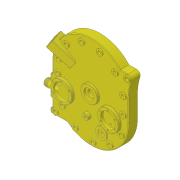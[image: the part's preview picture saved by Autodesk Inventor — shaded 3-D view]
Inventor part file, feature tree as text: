
AUTODESK INVENTOR PART (.ipt)
format: ipt  version: 2016 (Build 200138000, 138)  size: 1,254,400 bytes
history: native  units: in
note: dims shown in document units (in); Inventor stores cm internally (conversion verified against a paired STEP export)
features: thread x17
ambient origin geometry x8: Origin, YZ Plane, XZ Plane, XY Plane, X Axis, Y Axis, Z Axis, Center Point
bodies: Solid2 (feature_tree), Solid1 (feature_tree)
feature tree (17):
  thread  "Thread1"  [1 undecoded]
  thread  "Thread2"  [1 undecoded]
  thread  "Thread3"  [1 undecoded]
  thread  "Thread4"  [1 undecoded]
  thread  "Thread5"  [1 undecoded]
  thread  "Thread6"  [1 undecoded]
  thread  "Thread7"  [1 undecoded]
  thread  "Thread8"  [1 undecoded]
  thread  "Thread9"  [1 undecoded]
  thread  "Thread10"  [1 undecoded]
  thread  "Thread11"  [1 undecoded]
  thread  "Thread12"  [1 undecoded]
  thread  "Thread13"  [1 undecoded]
  thread  "Thread14"  [1 undecoded]
  thread  "Thread15"  [1 undecoded]
  thread  "Thread16"  [1 undecoded]
  thread  "Thread17"  [1 undecoded]
note: 17 required parameter values undecoded (feature->parameter linkage not recoverable at this tier; creation-order binding heuristic only, values carry confidence <= 0.55)
